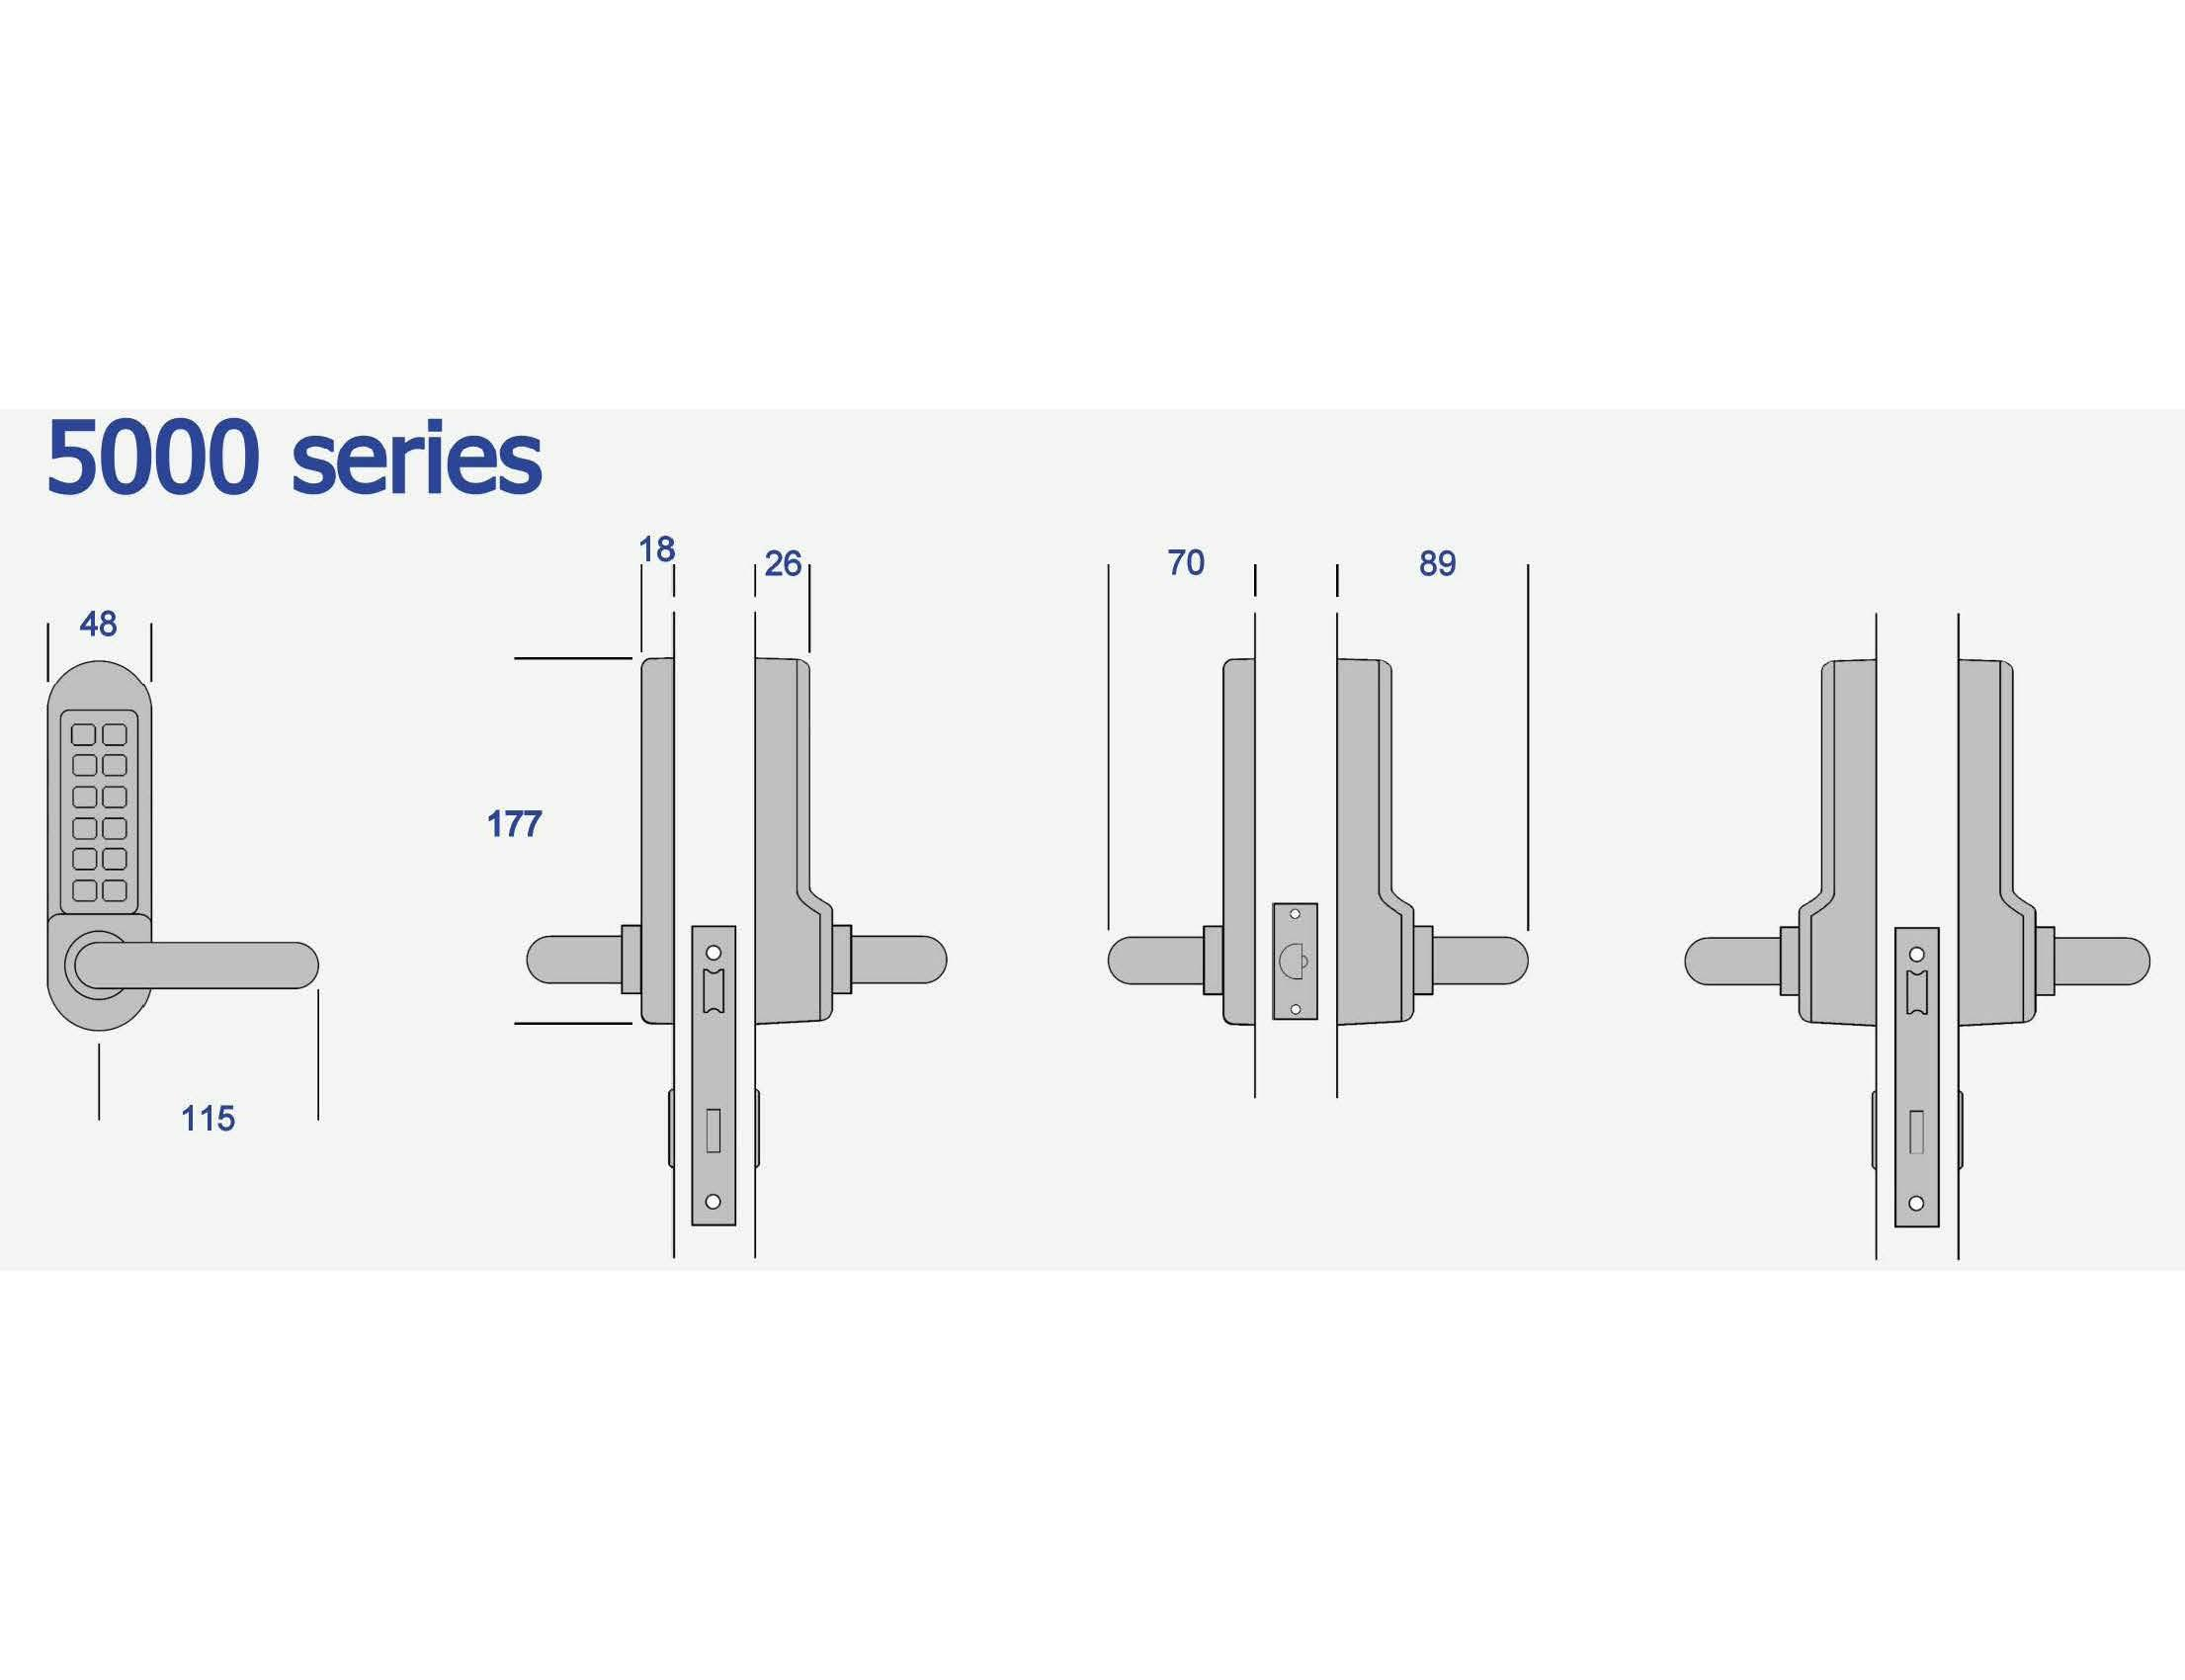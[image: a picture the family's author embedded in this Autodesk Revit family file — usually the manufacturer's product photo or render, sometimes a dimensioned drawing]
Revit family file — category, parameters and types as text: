
# Revit family: NBS_Lomax_Door_FDIN1-S
name_source: partatom
category: Doors
revit_build: Autodesk Revit Architecture 2016 (Build: 20150220_1215(x64)
units: mm (PartAtom-declared; Revit-internal decimal feet)

## family parameters
Always vertical = Yes
Cut with Voids When Loaded = No
Host = Wall
OmniClass Number = 23.30.10.00
OmniClass Title = Doors
Room Calculation Point = No
Shared = No

## types (1)
- NBS_Lomax_Door_FDIN1-S
    BIMObjectName = NBS_Lomax_Door_FDIN1-S
    Category = Doors
    Description = French Doors
    Frame Projection Ext. = 25 mm  [stored 0.082021 ft]
    Frame Projection Int. = 25 mm  [stored 0.082021 ft]
    Frame Width = 76 mm
    Function = Interior
    Glass = Glass
    Height = 2240 mm  [stored 7.34908 ft]
    Higes = Yes
    Hinges = Yes
    Lever Height from FFL = 1000 mm  [stored 3.28084 ft]
    Manufacturer = Lomax
    ManufacturerName = Lomax
    ManufacturerURL = lomaxwood.co.uk
    Model = NBS_Lomax_Door_FDIN1-S
    ModelNumber = FDIN1-S
    ModelReference = NBS_Lomax_Door_FDIN1-S
    NBSDescription = French Doors
    NBSNote = FDIN1-S
    NBSReference = NBS_Lomax_Door_FDIN1-S
    Name = FDIN1-S
    NominalHeight = 2240 mm  [stored 7.34908 ft]
    NominalLength = 76 mm
    NominalWidth = 1480 mm  [stored 4.85564 ft]
    ProductInformation = French Doors
    Revision = 1
    Rough Height = 2240 mm  [stored 7.34908 ft]
    Rough Width = 620 mm
    Thickness = 76 mm
    URL = lomaxwood.co.uk
    Wall Closure = By host
    White Wood = WHite Wood
    Width = 1480 mm  [stored 4.85564 ft]
    Wood Wood = Wood Wood

note: [stored X ft] marks values corroborated as IEEE doubles in the binary element streams (Revit-internal decimal feet)

## geometry (parser evidence)
native form markers: Blend x2, Sweep x18
no freeform markers — native parametric forms only
